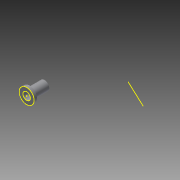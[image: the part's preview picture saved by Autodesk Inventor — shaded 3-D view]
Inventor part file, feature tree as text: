
AUTODESK INVENTOR PART (.ipt)
format: ipt  version: 2013 (Build 170138000, 138)  size: 74,752 bytes
history: native  units: in
note: dims shown in document units (in); Inventor stores cm internally (conversion verified against a paired STEP export)
features: other x2, sketch x1, imported_body x1, reference x1
ambient origin geometry x8: Origin, YZ Plane, XZ Plane, XY Plane, X Axis, Y Axis, Z Axis, Center Point
feature tree (5):
  other  "Boss-Extrude2"
  other  "AM-2235 threaded insert1"
  sketch  "Sketch1"
  imported_body  "Base1"
  reference  "Reference1"
